# Revit family: PLM-WCS-AEC-Water_Closet
name_source: partatom
category: Plumbing Fixtures
revit_build: Autodesk Revit 2016 (Build: 20150220_1215(x64)
units: mm (PartAtom-declared; Revit-internal decimal feet)

## family parameters
Always vertical = Yes
Cut with Voids When Loaded = No
OmniClass Number = 23.45.05.21.11
OmniClass Title = Water Closets
Part Type = Normal
Room Calculation Point = No
Round Connector Dimension = Use Diameter
Shared = Yes
Work Plane-Based = No

## types (1)
- Standard
    Bowl/Basin Material = Porcelain - Linen
    Drain Connection Diameter = 32 mm  [stored 0.104987 ft]
    Litres of Full Flush = 6
    Litres of Half Flush = 3
    Nominal Diameter = 16  [stored 0.0524934 ft]
    Seat Material = Laminate - Linen, Matte
    Show Yellow Background = Yes

note: [stored X ft] marks values corroborated as IEEE doubles in the binary element streams (Revit-internal decimal feet)

## geometry (parser evidence)
native form markers: Sweep x1
no freeform markers — native parametric forms only
